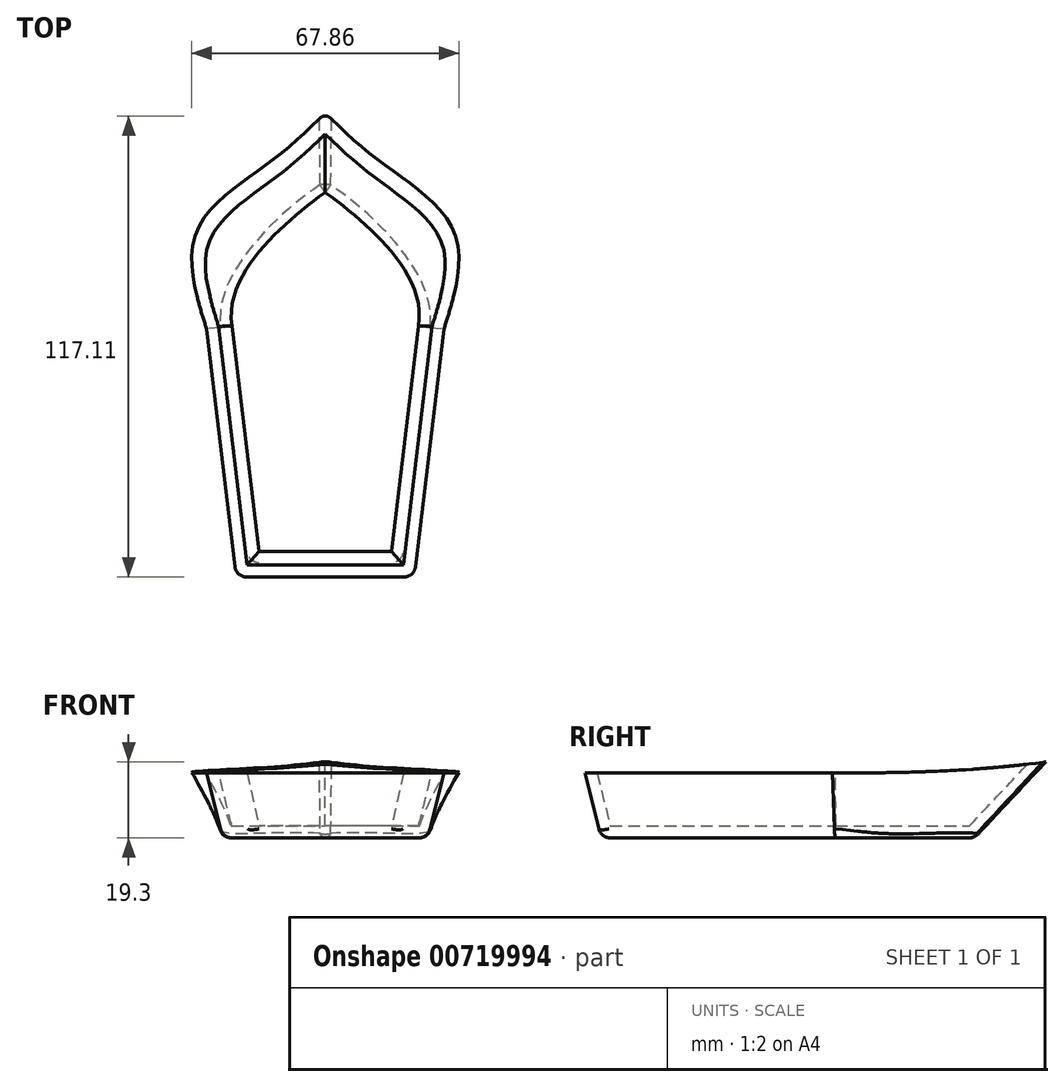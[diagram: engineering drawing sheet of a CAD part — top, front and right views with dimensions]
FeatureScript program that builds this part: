
annotation { "Feature Type Name" : "Feature", "Feature Type Description" : "" }
export const myFeature = defineFeature(function(context is Context, id is Id, definition is map)
    precondition{}
    {
        {
            var Q0;
            Q0=qCreatedBy(makeId("Top.planeOp"),FACE);
            var sketch = newSketch(context, id + "F0", { "sketchPlane" : qUnion([Q0])});
            skLineSegment(sketch, "E0", {"start": v(0, -22.49) * mm, "end": v(18.94, -22.49) * mm});
            skLineSegment(sketch, "E1", {"start": v(18.94, -22.49) * mm, "end": v(26.03, 36.86) * mm});
            skFitSpline(sketch, "E2", {"points": [v(26.03, 36.86) * mm, v(0, 72.87) * mm], "startDerivative": vector(2.8, 38.07) * mm, "endDerivative": vector(-40.59, 27.43) * mm});
            skLineSegment(sketch, "E3", {"start": v(0, 60) * mm, "end": v(0, 10.36) * mm, "construction": true});
            skFitSpline(sketch, "E4.MirrorCS", {"points": [v(-26.03, 36.86) * mm, v(0, 72.87) * mm], "startDerivative": vector(-2.8, 38.07) * mm, "endDerivative": vector(40.59, 27.43) * mm});
            skLineSegment(sketch, "E5.MirrorCS", {"start": v(-18.94, -22.49) * mm, "end": v(-26.03, 36.86) * mm});
            skLineSegment(sketch, "E6.MirrorCS", {"start": v(0, -22.49) * mm, "end": v(-18.94, -22.49) * mm});
            skLineSegment(sketch, "E7.0", {"start": v(23.38, -27.49) * mm, "end": v(31, 36.26) * mm});
            skLineSegment(sketch, "E8.0", {"start": v(0, -27.49) * mm, "end": v(23.38, -27.49) * mm});
            skFitSpline(sketch, "E9", {"points": [v(31, 36.26) * mm, v(0, 91.94) * mm], "startDerivative": vector(10.65, 80.97) * mm, "endDerivative": vector(-43.47, 34.59) * mm});
            skFitSpline(sketch, "E10.MirrorCS", {"points": [v(-31, 36.26) * mm, v(0, 91.94) * mm], "startDerivative": vector(-10.65, 80.97) * mm, "endDerivative": vector(43.47, 34.59) * mm});
            skLineSegment(sketch, "E11.MirrorCS", {"start": v(-23.38, -27.49) * mm, "end": v(-31, 36.26) * mm});
            skLineSegment(sketch, "E12.MirrorCS", {"start": v(0, -27.49) * mm, "end": v(-23.38, -27.49) * mm});
            skSolve(sketch);
        }
        {
            var Q0;
            Q0=qCreatedBy(makeId("Top.planeOp"),FACE);
            cPlane(context, id + "F1", {"entities" : qUnion([Q0]), "cplaneType" : CPlaneType.OFFSET, "offset" : 20 * mm, "width" : 150 * mm, "height" : 150 * mm});
        }
        {
            var Q0;
            Q0=qCreatedBy(id+"F1.planeOp",FACE);
            var sketch = newSketch(context, id + "F2", { "sketchPlane" : qUnion([Q0])});
            skFitSpline(sketch, "E13.0", {"points": [v(-31, 36.26) * mm, v(-34.55, 63.25) * mm, v(-14.5, 80.4) * mm, v(0, 91.94) * mm]});
            skFitSpline(sketch, "E14.0", {"points": [v(31, 36.26) * mm, v(34.55, 63.25) * mm, v(14.5, 80.4) * mm, v(0, 91.94) * mm]});
            skLineSegment(sketch, "E15.0", {"start": v(23.38, -27.49) * mm, "end": v(31, 36.26) * mm});
            skLineSegment(sketch, "E16.0", {"start": v(0, -27.49) * mm, "end": v(23.38, -27.49) * mm});
            skLineSegment(sketch, "E17.0", {"start": v(0, -27.49) * mm, "end": v(-23.38, -27.49) * mm});
            skPoint(sketch, "E18.0", {"position": v(-27.19, 4.39) * mm});
            skLineSegment(sketch, "E19.0", {"start": v(-23.38, -27.49) * mm, "end": v(-31, 36.26) * mm});
            skSolve(sketch);
        }
        {
            var Q0;
            Q0=makeQuery(id+"F0.imprint","IMPRINT",FACE,{"disambiguationData":[TD([[makeQuery(id+"F0.imprint","IMPRINT",EDGE,{"derivedFrom":sQuery(id+"F0.wireOp",EDGE,"E0")}),1.0]])]});
            var Q1;
            Q1=makeQuery(id+"F2.imprint","IMPRINT",FACE,{"disambiguationData":[TD([[makeQuery(id+"F2.imprint","IMPRINT",EDGE,{"derivedFrom":sQuery(id+"F2.wireOp",EDGE,"E13.0")}),-1.0]])]});
            loft(context, id + "F3", {"sheetProfilesArray" : [{ "sheetProfileEntities" : qUnion([Q0]) }, { "sheetProfileEntities" : qUnion([Q1]) }]});
        }
        {
            var Q0;
            Q0=makeQuery(id+"F3.opLoft","MID_CAP_EDGE",EDGE,{"disambiguationData":[OSD([sQuery(id+"F0.wireOp",EDGE,"E0"),sQuery(id+"F0.wireOp",EDGE,"E1"),sQuery(id+"F0.wireOp",EDGE,"E2")])],"capPos":0.0});
            var Q1;
            Q1=makeQuery(id+"F3.opLoft","MID_CAP_EDGE",EDGE,{"disambiguationData":[OSD([sQuery(id+"F0.wireOp",EDGE,"E1"),sQuery(id+"F0.wireOp",EDGE,"E2"),sQuery(id+"F0.wireOp",EDGE,"E4.MirrorCS")])],"capPos":0.0});
            var Q2;
            Q2=makeQuery(id+"F3.opLoft","MID_CAP_EDGE",EDGE,{"disambiguationData":[OSD([sQuery(id+"F0.wireOp",EDGE,"E2"),sQuery(id+"F0.wireOp",EDGE,"E4.MirrorCS"),sQuery(id+"F0.wireOp",EDGE,"E5.MirrorCS")])],"capPos":0.0});
            var Q3;
            Q3=makeQuery(id+"F3.opLoft","MID_CAP_EDGE",EDGE,{"disambiguationData":[OSD([sQuery(id+"F0.wireOp",EDGE,"E4.MirrorCS"),sQuery(id+"F0.wireOp",EDGE,"E5.MirrorCS"),sQuery(id+"F0.wireOp",EDGE,"E6.MirrorCS")])],"capPos":0.0});
            var Q4;
            Q4=makeQuery(id+"F3.opLoft","MID_CAP_EDGE",EDGE,{"disambiguationData":[OSD([sQuery(id+"F0.wireOp",EDGE,"E0"),sQuery(id+"F0.wireOp",EDGE,"E5.MirrorCS"),sQuery(id+"F0.wireOp",EDGE,"E6.MirrorCS")])],"capPos":0.0});
            var Q5;
            Q5=makeQuery(id+"F3.opLoft","SWEPT_EDGE",EDGE,{"disambiguationData":[OSD([sQuery(id+"F0.wireOp",EDGE,"E2"),sQuery(id+"F0.wireOp",EDGE,"E4.MirrorCS"),sQuery(id+"F2.wireOp",EDGE,"E13.0"),sQuery(id+"F2.wireOp",EDGE,"E14.0")])]});
            var Q6;
            Q6=makeQuery(id+"F3.opLoft","SWEPT_EDGE",EDGE,{"disambiguationData":[OSD([sQuery(id+"F0.wireOp",EDGE,"E0"),sQuery(id+"F0.wireOp",EDGE,"E1"),sQuery(id+"F2.wireOp",EDGE,"E15.0"),sQuery(id+"F2.wireOp",EDGE,"E16.0")])]});
            var Q7;
            Q7=makeQuery(id+"F3.opLoft","SWEPT_EDGE",EDGE,{"disambiguationData":[OSD([sQuery(id+"F0.wireOp",EDGE,"E5.MirrorCS"),sQuery(id+"F0.wireOp",EDGE,"E6.MirrorCS"),sQuery(id+"F2.wireOp",EDGE,"E17.0"),sQuery(id+"F2.wireOp",EDGE,"E19.0")])]});
            fillet(context, id + "F4", {"entities" : qUnion([Q0, Q1, Q2, Q3, Q4, Q5, Q6, Q7]), "radius" : 3 * mm, "tangentPropagation" : true, "allowEdgeOverflow" : false});
        }
        {
            var Q0;
            Q0=makeQuery(id+"F3.opLoft","CAP_FACE",FACE,{"disambiguationData":[OSD([makeQuery(id+"F2.imprint","IMPRINT",FACE,{"disambiguationData":[TD([[makeQuery(id+"F2.imprint","IMPRINT",EDGE,{"derivedFrom":sQuery(id+"F2.wireOp",EDGE,"E13.0")}),-1.0]])]})])],"isStart":true});
            shell(context, id + "F5", {"entities" : qUnion([Q0]), "thickness" : 3 * mm});
        }
        {
            var Q0;
            Q0=qCreatedBy(makeId("Right.planeOp"),FACE);
            var sketch = newSketch(context, id + "F6", { "sketchPlane" : qUnion([Q0])});
            skLineSegment(sketch, "E20", {"start": v(-30.69, 16.52) * mm, "end": v(44.7, 16.52) * mm});
            skFitSpline(sketch, "E21", {"points": [v(44.7, 16.52) * mm, v(93.74, 19.73) * mm], "startDerivative": vector(57.65, 0.49) * mm, "endDerivative": vector(48.89, 6.8) * mm});
            skLineSegment(sketch, "E22", {"start": v(-30.69, 16.52) * mm, "end": v(-30.69, 28.63) * mm});
            skLineSegment(sketch, "E23", {"start": v(-30.69, 28.63) * mm, "end": v(93.74, 28.63) * mm});
            skLineSegment(sketch, "E24", {"start": v(93.74, 28.63) * mm, "end": v(93.74, 19.73) * mm});
            skSolve(sketch);
        }
        {
            var Q0;
            Q0 = qSketchRegion(id + "F6", true);
            extrude(context, id + "F7", {"entities" : qUnion([Q0]), "operationType" : NewBodyOperationType.REMOVE, "endBound" : BoundingType.SYMMETRIC, "oppositeDirection" : true, "depth" : 80 * mm, "offsetDistance" : 25 * mm});
        }
    });
